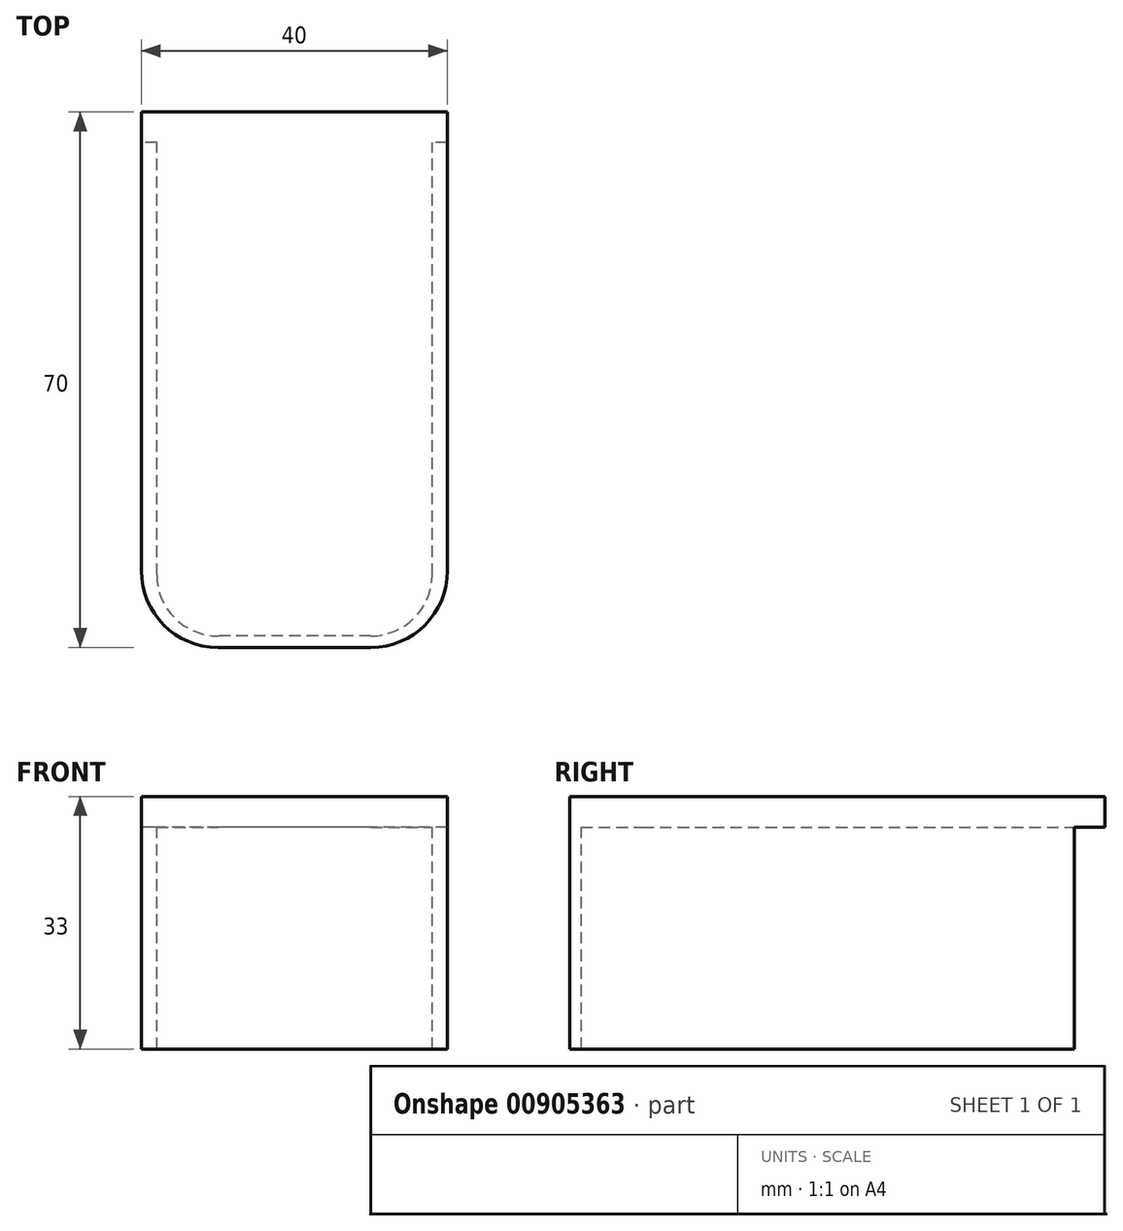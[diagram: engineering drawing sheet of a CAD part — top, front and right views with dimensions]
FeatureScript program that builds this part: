
annotation { "Feature Type Name" : "Feature", "Feature Type Description" : "" }
export const myFeature = defineFeature(function(context is Context, id is Id, definition is map)
    precondition{}
    {
        {
            var Q0;
            Q0=qCreatedBy(makeId("Top.planeOp"),FACE);
            var sketch = newSketch(context, id + "F0", { "sketchPlane" : qUnion([Q0])});
            skLineSegment(sketch, "E0.bottom", {"start": v(10.16, -35.1) * mm, "end": v(-9.84, -35.1) * mm});
            skLineSegment(sketch, "E0.top", {"start": v(20.16, 34.9) * mm, "end": v(-19.84, 34.9) * mm});
            skLineSegment(sketch, "E0.left", {"start": v(20.16, -25.1) * mm, "end": v(20.16, 34.9) * mm});
            skLineSegment(sketch, "E0.right", {"start": v(-19.84, -25.1) * mm, "end": v(-19.84, 34.9) * mm});
            skPoint(sketch, "E0.middle", {"position": v(0.16, -0.1) * mm});
            skLineSegment(sketch, "E1.0", {"start": v(15.16, -25.6) * mm, "end": v(15.16, 30.9) * mm});
            skLineSegment(sketch, "E2.0", {"start": v(-14.84, -25.6) * mm, "end": v(-14.84, 30.9) * mm});
            skLineSegment(sketch, "E3.0", {"start": v(10.16, -30.6) * mm, "end": v(-9.84, -30.6) * mm});
            skArc(sketch, "E4.filletArc", {"start": v(-14.84, -25.6) * mm, "mid": v(-13.37, -29.13) * mm, "end": v(-9.84, -30.6) * mm});
            skArc(sketch, "E5.filletArc", {"start": v(10.16, -30.6) * mm, "mid": v(13.7, -29.13) * mm, "end": v(15.16, -25.6) * mm});
            skPoint(sketch, "E6.visualSharp", {"position": v(20.16, -35.1) * mm});
            skArc(sketch, "E6.filletArc", {"start": v(10.16, -35.1) * mm, "mid": v(17.23, -32.17) * mm, "end": v(20.16, -25.1) * mm});
            skPoint(sketch, "E7.visualSharp", {"position": v(-19.84, -35.1) * mm});
            skArc(sketch, "E7.filletArc", {"start": v(-19.84, -25.1) * mm, "mid": v(-16.9, -32.17) * mm, "end": v(-9.84, -35.1) * mm});
            skLineSegment(sketch, "E8.0", {"start": v(-16.84, -25.6) * mm, "end": v(-16.84, 30.9) * mm});
            skLineSegment(sketch, "E9.0", {"start": v(17.16, -25.6) * mm, "end": v(17.16, 30.9) * mm});
            skArc(sketch, "E10.0", {"start": v(10.16, -32.6) * mm, "mid": v(15.11, -30.55) * mm, "end": v(17.16, -25.6) * mm});
            skLineSegment(sketch, "E11.0", {"start": v(10.16, -32.6) * mm, "end": v(-9.84, -32.6) * mm});
            skArc(sketch, "E12.0", {"start": v(-16.84, -25.6) * mm, "mid": v(-14.79, -30.55) * mm, "end": v(-9.84, -32.6) * mm});
            skLineSegment(sketch, "E13.0", {"start": v(-17.84, -25.6) * mm, "end": v(-17.84, 30.9) * mm});
            skLineSegment(sketch, "E13.1", {"start": v(18.16, -25.6) * mm, "end": v(18.16, 30.9) * mm});
            skArc(sketch, "E13.2", {"start": v(10.16, -33.6) * mm, "mid": v(15.82, -31.25) * mm, "end": v(18.16, -25.6) * mm});
            skLineSegment(sketch, "E13.3", {"start": v(10.16, -33.6) * mm, "end": v(-9.84, -33.6) * mm});
            skArc(sketch, "E13.4", {"start": v(-17.84, -25.6) * mm, "mid": v(-15.5, -31.25) * mm, "end": v(-9.84, -33.6) * mm});
            skLineSegment(sketch, "E14.0", {"start": v(20.16, 30.9) * mm, "end": v(-19.84, 30.9) * mm});
            skSolve(sketch);
        }
        {
            var Q0;
            Q0=makeQuery(id+"F0.imprint","IMPRINT",FACE,{"disambiguationData":[TD([[makeQuery(id+"F0.imprint","IMPRINT",EDGE,{"derivedFrom":sQuery(id+"F0.wireOp",EDGE,"E0.bottom")}),-1.0]])]});
            var Q1;
            {var subQ1=sQuery(id+"F0.wireOp",EDGE,"E0.top");Q1=makeQuery(id+"F0.imprint","IMPRINT",FACE,{"disambiguationData":[TD([[makeQuery(id+"F0.imprint","IMPRINT",EDGE,{"derivedFrom":subQ1}),1.0]])]});}
            var Q2;
            {var subQ2=sQuery(id+"F0.wireOp",EDGE,"E8.0");Q2=makeQuery(id+"F0.imprint","IMPRINT",FACE,{"disambiguationData":[TD([[makeQuery(id+"F0.imprint","IMPRINT",EDGE,{"derivedFrom":subQ2}),1.0]])]});}
            var Q3;
            {var subQ1=sQuery(id+"F0.wireOp",EDGE,"E1.0");Q3=makeQuery(id+"F0.imprint","IMPRINT",FACE,{"disambiguationData":[TD([[makeQuery(id+"F0.imprint","IMPRINT",EDGE,{"derivedFrom":subQ1}),1.0]])]});}
            var Q4;
            {var subQ2=sQuery(id+"F0.wireOp",EDGE,"E1.0");Q4=makeQuery(id+"F0.imprint","IMPRINT",FACE,{"disambiguationData":[TD([[makeQuery(id+"F0.imprint","IMPRINT",EDGE,{"derivedFrom":subQ2}),-1.0]])]});}
            extrude(context, id + "F1", {"entities" : qUnion([Q0, Q1, Q2, Q3, Q4]), "depth" : 4 * mm, "offsetDistance" : 25 * mm});
        }
        {
            var Q0;
            Q0=makeQuery(id+"F0.imprint","IMPRINT",FACE,{"disambiguationData":[TD([[makeQuery(id+"F0.imprint","IMPRINT",EDGE,{"derivedFrom":sQuery(id+"F0.wireOp",EDGE,"E0.bottom")}),-1.0]])]});
            extrude(context, id + "F2", {"entities" : qUnion([Q0]), "operationType" : NewBodyOperationType.ADD, "oppositeDirection" : true, "depth" : 29 * mm, "offsetDistance" : 25 * mm});
        }
    });
